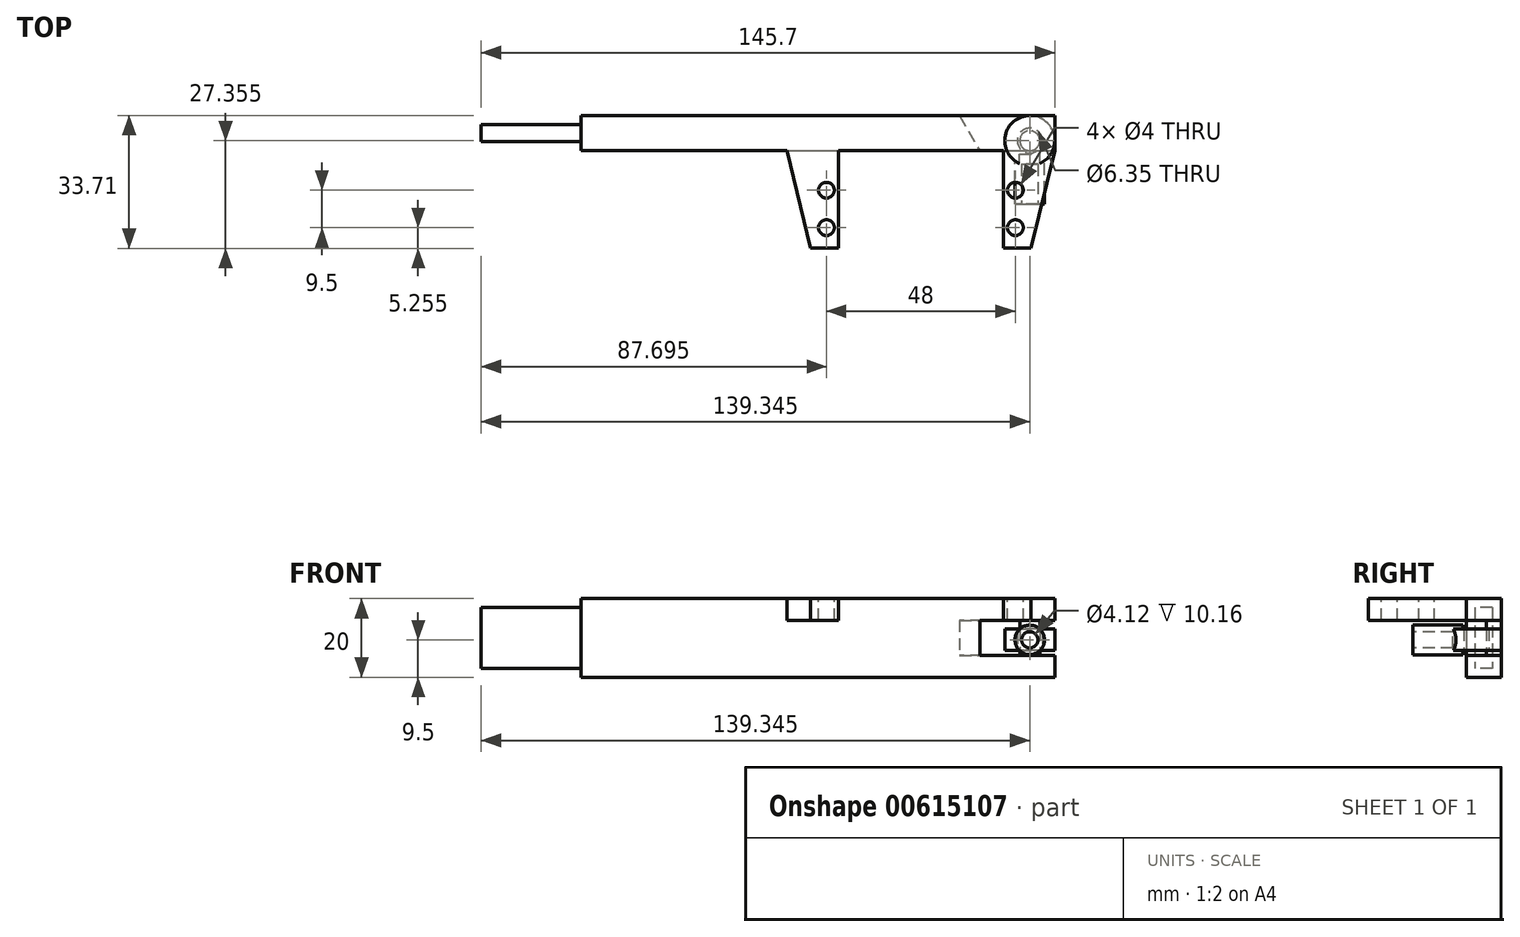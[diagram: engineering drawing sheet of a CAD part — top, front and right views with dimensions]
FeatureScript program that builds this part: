
annotation { "Feature Type Name" : "Feature", "Feature Type Description" : "" }
export const myFeature = defineFeature(function(context is Context, id is Id, definition is map)
    precondition{}
    {
        {
            var Q0;
            Q0=qCreatedBy(makeId("Top.planeOp"),FACE);
            var sketch = newSketch(context, id + "F0", { "sketchPlane" : qUnion([Q0])});
            skLineSegment(sketch, "E0.bottom", {"start": v(-60.15, 4.45) * mm, "end": v(60.15, 4.45) * mm});
            skLineSegment(sketch, "E0.top", {"start": v(-60.15, -4.44) * mm, "end": v(60.15, -4.44) * mm});
            skLineSegment(sketch, "E0.left", {"start": v(-60.15, 4.45) * mm, "end": v(-60.15, -4.44) * mm});
            skLineSegment(sketch, "E0.right", {"start": v(60.15, 4.45) * mm, "end": v(60.15, -4.44) * mm});
            skPoint(sketch, "E0.middle", {"position": v(0, 0) * mm});
            skSolve(sketch);
        }
        {
            var Q0;
            Q0 = qSketchRegion(id + "F0", true);
            extrude(context, id + "F1", {"entities" : qUnion([Q0]), "endBound" : BoundingType.SYMMETRIC, "depth" : 20 * mm, "offsetDistance" : 25.4 * mm});
        }
        {
            var Q0;
            Q0=makeQuery(id+"F1.opExtrude","SWEPT_FACE",FACE,{"disambiguationData":[OSD([sQuery(id+"F0.wireOp",EDGE,"E0.left")])]});
            var sketch = newSketch(context, id + "F2", { "sketchPlane" : qUnion([Q0])});
            skLineSegment(sketch, "E1.bottom", {"start": v(-2.2, 7.75) * mm, "end": v(2.2, 7.75) * mm});
            skLineSegment(sketch, "E1.top", {"start": v(-2.2, -7.75) * mm, "end": v(2.2, -7.75) * mm});
            skLineSegment(sketch, "E1.left", {"start": v(-2.2, 7.75) * mm, "end": v(-2.2, -7.75) * mm});
            skLineSegment(sketch, "E1.right", {"start": v(2.2, 7.75) * mm, "end": v(2.2, -7.75) * mm});
            skPoint(sketch, "E1.middle", {"position": v(0, 0) * mm});
            skSolve(sketch);
        }
        {
            var Q0;
            Q0 = qSketchRegion(id + "F2", true);
            extrude(context, id + "F3", {"entities" : qUnion([Q0]), "operationType" : NewBodyOperationType.ADD, "depth" : 25.4 * mm, "offsetDistance" : 25.4 * mm});
        }
        {
            var Q0;
            Q0=makeQuery(id+"F1.opExtrude","SWEPT_FACE",FACE,{"disambiguationData":[OSD([sQuery(id+"F0.wireOp",EDGE,"E0.top")])]});
            var sketch = newSketch(context, id + "F4", { "sketchPlane" : qUnion([Q0])});
            skLineSegment(sketch, "E2.bottom", {"start": v(41.1, 4.5) * mm, "end": v(60.15, 4.5) * mm});
            skLineSegment(sketch, "E2.top", {"start": v(41.1, -4.5) * mm, "end": v(60.15, -4.5) * mm});
            skLineSegment(sketch, "E2.left", {"start": v(41.1, 4.5) * mm, "end": v(41.1, -4.5) * mm});
            skLineSegment(sketch, "E2.right", {"start": v(60.15, 4.5) * mm, "end": v(60.15, -4.5) * mm});
            skPoint(sketch, "E2.middle", {"position": v(50.62, 0) * mm});
            skSolve(sketch);
        }
        {
            var Q0;
            Q0 = qSketchRegion(id + "F4", true);
            extrude(context, id + "F5", {"entities" : qUnion([Q0]), "operationType" : NewBodyOperationType.REMOVE, "endBound" : BoundingType.THROUGH_ALL, "oppositeDirection" : true, "depth" : 25.4 * mm, "offsetDistance" : 25.4 * mm});
        }
        {
            var Q0;
            Q0=makeQuery(id+"F5.boolean.opBoolean","COPY",FACE,{"derivedFrom":makeQuery(id+"F5.opExtrude","SWEPT_FACE",FACE,{"disambiguationData":[OSD([sQuery(id+"F4.wireOp",EDGE,"E2.top")])]})});
            var sketch = newSketch(context, id + "F6", { "sketchPlane" : qUnion([Q0])});
            skCircle(sketch, "E3", {"center": v(53.8, -1.9) * mm, "radius": 2.54 * mm});
            skSolve(sketch);
        }
        {
            var Q0;
            Q0 = qSketchRegion(id + "F6", true);
            extrude(context, id + "F7", {"entities" : qUnion([Q0]), "operationType" : NewBodyOperationType.ADD, "endBound" : BoundingType.UP_TO_NEXT, "depth" : 25.4 * mm, "offsetDistance" : 25.4 * mm});
        }
        {
            var Q0;
            Q0=makeQuery(id+"F5.boolean.opBoolean","COPY",FACE,{"derivedFrom":makeQuery(id+"F5.opExtrude","SWEPT_FACE",FACE,{"disambiguationData":[OSD([sQuery(id+"F4.wireOp",EDGE,"E2.top")])]})});
            cPlane(context, id + "F8", {"entities" : qUnion([Q0]), "cplaneType" : CPlaneType.OFFSET, "offset" : 1.27 * mm, "width" : 152.4 * mm, "height" : 152.4 * mm});
        }
        {
            var Q0;
            Q0=qCreatedBy(id+"F8.planeOp",FACE);
            var sketch = newSketch(context, id + "F9", { "sketchPlane" : qUnion([Q0])});
            skCircle(sketch, "E4.0", {"center": v(53.8, -1.9) * mm, "radius": 2.54 * mm});
            skCircle(sketch, "E5", {"center": v(53.8, -1.9) * mm, "radius": 3.17 * mm});
            skLineSegment(sketch, "E6.0", {"start": v(60.15, 4.45) * mm, "end": v(41.1, 4.45) * mm});
            skCircle(sketch, "E7", {"center": v(53.8, -1.9) * mm, "radius": 6.35 * mm});
            skSolve(sketch);
        }
        {
            var Q0;
            Q0 = qSketchRegion(id + "F9", true);
            extrude(context, id + "F10", {"entities" : qUnion([Q0]), "depth" : 8 * mm - 2.54 * mm, "offsetDistance" : 25.4 * mm});
        }
        {
            var Q0;
            Q0=makeQuery(id+"F1.opExtrude","SWEPT_FACE",FACE,{"disambiguationData":[OSD([sQuery(id+"F0.wireOp",EDGE,"E0.top")])]});
            cPlane(context, id + "F11", {"entities" : qUnion([Q0]), "cplaneType" : CPlaneType.OFFSET, "offset" : 0.89 * mm, "width" : 152.4 * mm, "height" : 152.4 * mm});
        }
        {
            var Q0;
            Q0=qCreatedBy(id+"F11.planeOp",FACE);
            var sketch = newSketch(context, id + "F12", { "sketchPlane" : qUnion([Q0])});
            skLineSegment(sketch, "E8.0.0", {"start": v(60.15, -3.23) * mm, "end": v(47.45, -3.23) * mm});
            skLineSegment(sketch, "E9.0.0", {"start": v(47.45, 2.23) * mm, "end": v(60.15, 2.23) * mm});
            skLineSegment(sketch, "E10", {"start": v(53.8, 2.23) * mm, "end": v(53.8, -3.23) * mm, "construction": true});
            skCircle(sketch, "E11", {"center": v(53.8, -0.5) * mm, "radius": 3.75 * mm});
            skSolve(sketch);
        }
        {
            var Q0;
            Q0 = qSketchRegion(id + "F12", true);
            extrude(context, id + "F13", {"entities" : qUnion([Q0]), "operationType" : NewBodyOperationType.ADD, "depth" : 12.7 * mm, "offsetDistance" : 25.4 * mm});
        }
        {
            var Q0;
            Q0=makeQuery(id+"F13.opExtrude","CAP_FACE",FACE,{"disambiguationData":[OSD([sQuery(id+"F12.wireOp",EDGE,"E11")])],"isStart":false});
            var sketch = newSketch(context, id + "F14", { "sketchPlane" : qUnion([Q0])});
            skCircle(sketch, "E12.0", {"center": v(53.8, -0.5) * mm, "radius": 3.75 * mm, "construction": true});
            skCircle(sketch, "E13", {"center": v(53.8, -0.5) * mm, "radius": 2.06 * mm});
            skSolve(sketch);
        }
        {
            var Q0;
            Q0 = qSketchRegion(id + "F14", true);
            extrude(context, id + "F15", {"entities" : qUnion([Q0]), "operationType" : NewBodyOperationType.REMOVE, "oppositeDirection" : true, "depth" : 10.16 * mm, "offsetDistance" : 25.4 * mm});
        }
        {
            var Q0;
            Q0=makeQuery(id+"F1.opExtrude","SWEPT_FACE",FACE,{"disambiguationData":[OSD([sQuery(id+"F0.wireOp",EDGE,"E0.top")])]});
            var sketch = newSketch(context, id + "F16", { "sketchPlane" : qUnion([Q0])});
            skLineSegment(sketch, "E14.bottom", {"start": v(-7.85, 10) * mm, "end": v(5.15, 10) * mm});
            skLineSegment(sketch, "E14.top", {"start": v(-7.85, 4.5) * mm, "end": v(5.15, 4.5) * mm});
            skLineSegment(sketch, "E14.left", {"start": v(-7.85, 10) * mm, "end": v(-7.85, 4.5) * mm});
            skLineSegment(sketch, "E14.right", {"start": v(5.15, 10) * mm, "end": v(5.15, 4.5) * mm});
            skLineSegment(sketch, "E15.bottom", {"start": v(47.15, 10) * mm, "end": v(60.15, 10) * mm});
            skLineSegment(sketch, "E15.top", {"start": v(47.15, 4.5) * mm, "end": v(60.15, 4.5) * mm});
            skLineSegment(sketch, "E15.left", {"start": v(47.15, 10) * mm, "end": v(47.15, 4.5) * mm});
            skLineSegment(sketch, "E15.right", {"start": v(60.15, 10) * mm, "end": v(60.15, 4.5) * mm});
            skSolve(sketch);
        }
        {
            var Q0;
            Q0 = qSketchRegion(id + "F16", true);
            extrude(context, id + "F17", {"entities" : qUnion([Q0]), "operationType" : NewBodyOperationType.ADD, "depth" : 21 * mm + 3.8 * mm, "offsetDistance" : 25.4 * mm});
        }
        {
            var Q0;
            Q0=makeQuery(id+"F17.boolean.opBoolean","MERGE",FACE,{"derivedFrom":[makeQuery(id+"F1.opExtrude","CAP_FACE",FACE,{"disambiguationData":[OSD([sQuery(id+"F0.wireOp",EDGE,"E0.bottom"),sQuery(id+"F0.wireOp",EDGE,"E0.top"),sQuery(id+"F0.wireOp",EDGE,"E0.left"),sQuery(id+"F0.wireOp",EDGE,"E0.right")])],"isStart":false}),makeQuery(id+"F17.opExtrude","SWEPT_FACE",FACE,{"disambiguationData":[OSD([sQuery(id+"F16.wireOp",EDGE,"E14.bottom")])]}),makeQuery(id+"F17.opExtrude","SWEPT_FACE",FACE,{"disambiguationData":[OSD([sQuery(id+"F16.wireOp",EDGE,"E15.bottom")])]})]});
            var sketch = newSketch(context, id + "F18", { "sketchPlane" : qUnion([Q0])});
            skLineSegment(sketch, "E16.0.0", {"start": v(-60.15, 4.45) * mm, "end": v(-60.15, -4.44) * mm, "construction": true});
            skLineSegment(sketch, "E16.0.1", {"start": v(-60.15, -4.44) * mm, "end": v(-7.85, -4.44) * mm, "construction": true});
            skLineSegment(sketch, "E16.0.2", {"start": v(-7.85, -4.45) * mm, "end": v(-7.85, -29.25) * mm, "construction": true});
            skLineSegment(sketch, "E16.0.3", {"start": v(-7.85, -29.25) * mm, "end": v(5.15, -29.25) * mm, "construction": true});
            skLineSegment(sketch, "E16.0.4", {"start": v(5.15, -29.25) * mm, "end": v(5.15, -4.45) * mm, "construction": true});
            skLineSegment(sketch, "E16.0.5", {"start": v(5.15, -4.44) * mm, "end": v(47.15, -4.44) * mm, "construction": true});
            skLineSegment(sketch, "E16.0.6", {"start": v(47.15, -4.45) * mm, "end": v(47.15, -29.25) * mm, "construction": true});
            skLineSegment(sketch, "E16.0.7", {"start": v(47.15, -29.25) * mm, "end": v(60.15, -29.25) * mm, "construction": true});
            skLineSegment(sketch, "E16.0.8", {"start": v(60.15, -29.25) * mm, "end": v(60.15, 4.45) * mm, "construction": true});
            skLineSegment(sketch, "E16.0.9", {"start": v(60.15, 4.45) * mm, "end": v(-60.15, 4.45) * mm, "construction": true});
            skLineSegment(sketch, "E17", {"start": v(-7.85, -4.44) * mm, "end": v(-7.85, -29.25) * mm});
            skLineSegment(sketch, "E18", {"start": v(-7.85, -29.25) * mm, "end": v(-1.85, -29.25) * mm});
            skLineSegment(sketch, "E19", {"start": v(-1.85, -29.25) * mm, "end": v(-7.85, -4.44) * mm});
            skLineSegment(sketch, "E20", {"start": v(60.15, -4.44) * mm, "end": v(60.15, -29.25) * mm});
            skLineSegment(sketch, "E21", {"start": v(60.15, -29.25) * mm, "end": v(54.15, -29.25) * mm});
            skLineSegment(sketch, "E22", {"start": v(54.15, -29.25) * mm, "end": v(60.15, -4.44) * mm});
            skSolve(sketch);
        }
        {
            var Q0;
            Q0 = qSketchRegion(id + "F18", true);
            extrude(context, id + "F19", {"entities" : qUnion([Q0]), "operationType" : NewBodyOperationType.REMOVE, "oppositeDirection" : true, "depth" : 6 * mm, "offsetDistance" : 25.4 * mm});
        }
        {
            var Q0;
            Q0=makeQuery(id+"F17.boolean.opBoolean","MERGE",FACE,{"derivedFrom":[makeQuery(id+"F1.opExtrude","CAP_FACE",FACE,{"disambiguationData":[OSD([sQuery(id+"F0.wireOp",EDGE,"E0.bottom"),sQuery(id+"F0.wireOp",EDGE,"E0.top"),sQuery(id+"F0.wireOp",EDGE,"E0.left"),sQuery(id+"F0.wireOp",EDGE,"E0.right")])],"isStart":false}),makeQuery(id+"F17.opExtrude","SWEPT_FACE",FACE,{"disambiguationData":[OSD([sQuery(id+"F16.wireOp",EDGE,"E14.bottom")])]}),makeQuery(id+"F17.opExtrude","SWEPT_FACE",FACE,{"disambiguationData":[OSD([sQuery(id+"F16.wireOp",EDGE,"E15.bottom")])]})]});
            var sketch = newSketch(context, id + "F20", { "sketchPlane" : qUnion([Q0])});
            skCircle(sketch, "E23", {"center": v(50.15, -24) * mm, "radius": 2 * mm});
            skCircle(sketch, "E24", {"center": v(50.15, -14.5) * mm, "radius": 2 * mm});
            skCircle(sketch, "E25", {"center": v(2.15, -24) * mm, "radius": 2 * mm});
            skCircle(sketch, "E26", {"center": v(2.15, -14.5) * mm, "radius": 2 * mm});
            skSolve(sketch);
        }
        {
            var Q0;
            Q0 = qSketchRegion(id + "F20", true);
            extrude(context, id + "F21", {"entities" : qUnion([Q0]), "operationType" : NewBodyOperationType.REMOVE, "oppositeDirection" : true, "depth" : 6 * mm, "offsetDistance" : 25.4 * mm});
        }
        {
            var Q0;
            Q0=makeQuery(id+"F5.boolean.opBoolean","COPY",FACE,{"derivedFrom":makeQuery(id+"F5.opExtrude","SWEPT_FACE",FACE,{"disambiguationData":[OSD([sQuery(id+"F4.wireOp",EDGE,"E2.top")])]})});
            var sketch = newSketch(context, id + "F22", { "sketchPlane" : qUnion([Q0])});
            skLineSegment(sketch, "E27", {"start": v(41.1, -4.44) * mm, "end": v(41.1, 4.45) * mm});
            skLineSegment(sketch, "E28", {"start": v(41.1, 4.45) * mm, "end": v(35.96, 4.45) * mm});
            skLineSegment(sketch, "E29", {"start": v(35.96, 4.45) * mm, "end": v(41.1, -4.44) * mm});
            skSolve(sketch);
        }
        {
            var Q0;
            Q0 = qSketchRegion(id + "F22", true);
            extrude(context, id + "F23", {"entities" : qUnion([Q0]), "operationType" : NewBodyOperationType.REMOVE, "depth" : 9 * mm, "offsetDistance" : 25.4 * mm});
        }
    });
